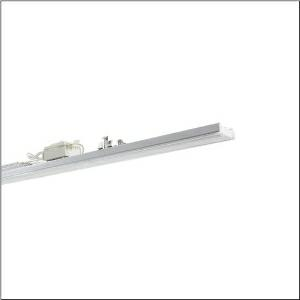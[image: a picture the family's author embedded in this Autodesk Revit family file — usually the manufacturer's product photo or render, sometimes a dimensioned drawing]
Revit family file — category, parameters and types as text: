
# Revit family: licross_r__21_recessed_mo_52tl19cn485g_b288
name_source: partatom
category: Lighting Fixtures
units: mm (PartAtom-declared; Revit-internal decimal feet)

## family parameters
Cut with Voids When Loaded = No
Host = Face
Light Source = No
Part Type = Normal
Room Calculation Point = No
Round Connector Dimension = Use Diameter
Shared = No

## types (1)
- --- (1 x LED, 8870 lm, 49.9 W, 4000K)
    Apparent Load = 50 VA
    CIE Flux Codes = 55 90 98 100 100
    Color Rendering = 80
    Color Temperature = 4000K
    Default Elevation = 1800 mm
    Description = Licross® 21 Recessed MO, luminaire insert, of sheet steel, galvanised, coil coated, white, length: 1.500mm, width: 66mm, height: 67mm, LED rated luminous flux: 8.880lm, light colour: 840, control gear: ON/OFF Multilumen, CLOi, control gear: ECG DALI, with plug, 5-pole, with phase selection, mains connection: 220..240V, AC, 50/60Hz, start of lifetime: 50W, end of service life: 61W, halogen-free wiring, primary light control with lens, of plastic, primary optical cover: cover, of PMMA, light emission: direct distribution, primary light characteristic: double asymmetric, protection rating (complete): IP40, insulation class (complete): insulation class I (protective earthing), certification: CE, ENEC, VDE, UKCA, protection symbol: D if used in an environment without relevant dust loads with corresponding accessories, impact resistance: IK06, permissible ambient temperature for indoor applications: -35..+40°C, corresponds to IFS (International Featured Standards) requirements for safety and quality in the food industry, reducing of maximum allowable ambient temperature of 5°C with ceiling mounting, LABS conformity tested according to VDMA 24364:2018-05, packaging unit: 1 piece
    Height = 58 mm
    Lamp = 1 x LED
    Lamp Light Flux = 8870 lm
    Lamp Power = 49.9 W
    Lamp count = 1
    Length = 1500 mm
    Luminous efficacy = 178 lm/W
    Manufacturer = Siteco
    ModVariant = No
    Model = 52TL19CN485G
    Mounting Place = Ceiling
    Mounting Type = Pendant
    Number of Poles = 1
    OnlyDefault = Yes
    Power Factor = 1
    Product Name = Licross® 21 Recessed MO
    Product group = luminaire insert
    ProductGroupID = 902
    Protection Class = Protection class I
    Protection Degree = IP 40
    RLX_Detail_Level = 1
    RLX_Emergency_Light_Flux = 0 lm
    RLX_Emergency_Type = 0
    RLX_Emergency_Type_DB = No
    RlxData = <blob elided: 22297 chars, md5=5ae9e5b9>
    Socket = socket
    Standby Power = 0 W
    System Light Flux = 8870 lm
    System Power = 50 W
    Type Comments = factory setting: luminous flux: 100 % | (A | C | E) | 116 mA
    Type Image = l_1296930.jpg
    URL = http://relux.com
    VarID = @adj_110814
    Voltage = 0 V
    Weight = 0.00 kg
    Width = 66 mm

## geometry (parser evidence)
native form markers: Blend x4, Sweep x11
no freeform markers — native parametric forms only
